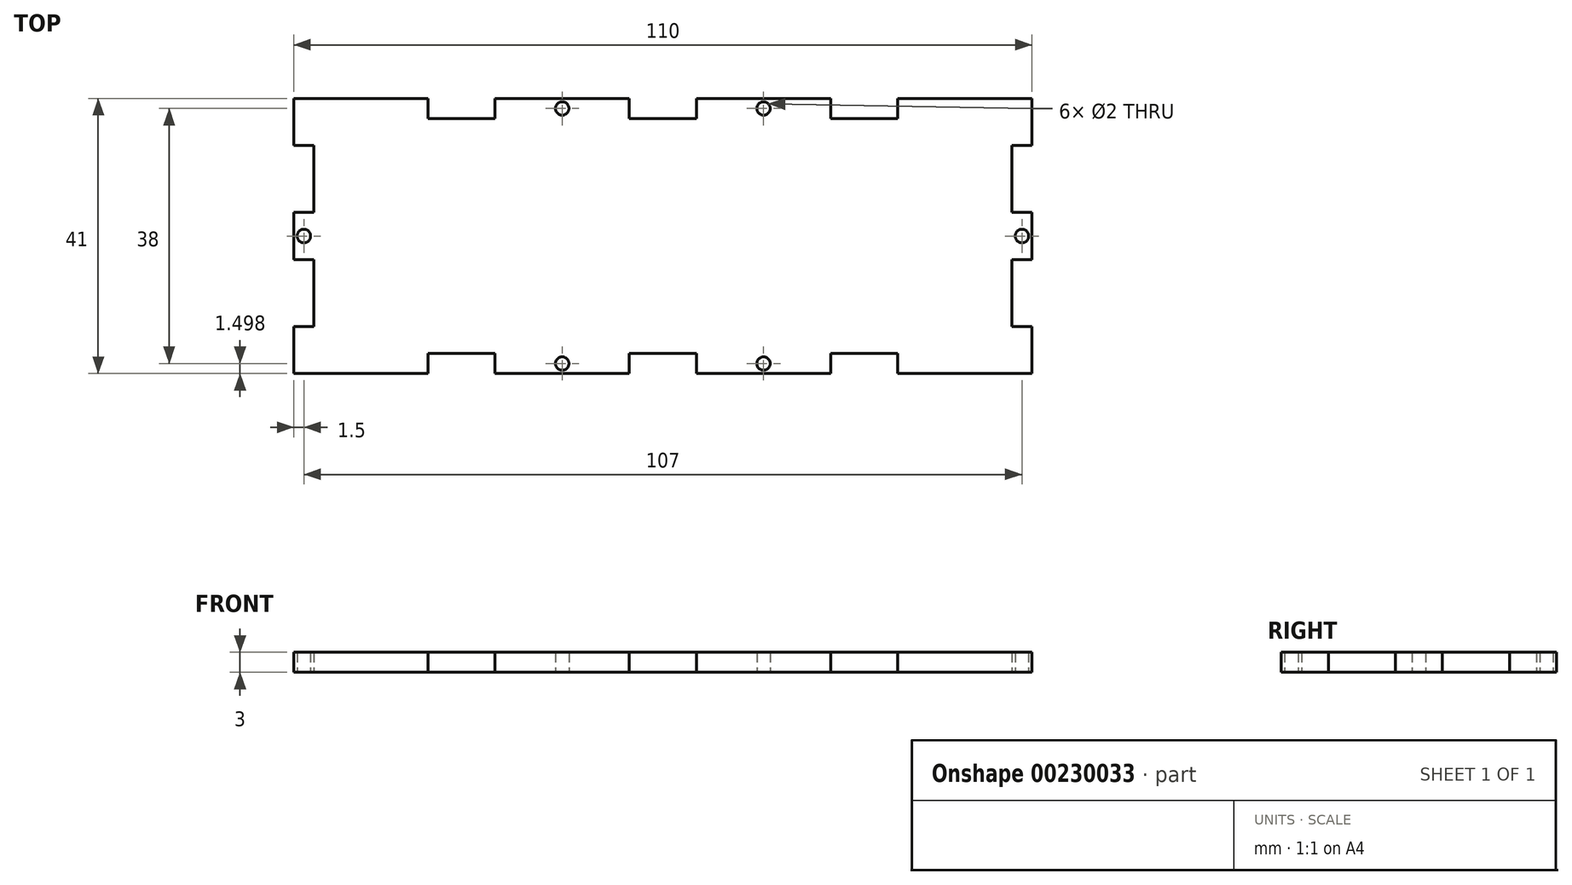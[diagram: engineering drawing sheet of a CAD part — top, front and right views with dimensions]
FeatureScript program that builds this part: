
annotation { "Feature Type Name" : "Feature", "Feature Type Description" : "" }
export const myFeature = defineFeature(function(context is Context, id is Id, definition is map)
    precondition{}
    {
        {
            var Q0;
            Q0=qCreatedBy(makeId("Top.planeOp"),FACE);
            var sketch = newSketch(context, id + "F0", { "sketchPlane" : qUnion([Q0])});
            skLineSegment(sketch, "E0", {"start": v(-55, 21.1) * mm, "end": v(-55, 14.1) * mm});
            skLineSegment(sketch, "E1", {"start": v(-55, 14.1) * mm, "end": v(-52, 14.1) * mm});
            skLineSegment(sketch, "E2", {"start": v(-52, 14.1) * mm, "end": v(-52, 4.1) * mm});
            skLineSegment(sketch, "E3", {"start": v(-52, 4.1) * mm, "end": v(-55, 4.1) * mm});
            skLineSegment(sketch, "E4", {"start": v(-55, 4.1) * mm, "end": v(-55, 0.6) * mm});
            skLineSegment(sketch, "E5", {"start": v(-55, 21.1) * mm, "end": v(-35, 21.1) * mm});
            skLineSegment(sketch, "E6", {"start": v(-35, 21.1) * mm, "end": v(-35, 18.1) * mm});
            skLineSegment(sketch, "E7", {"start": v(-35, 18.1) * mm, "end": v(-25, 18.1) * mm});
            skLineSegment(sketch, "E8", {"start": v(-25, 18.1) * mm, "end": v(-25, 21.1) * mm});
            skLineSegment(sketch, "E9", {"start": v(-25, 21.1) * mm, "end": v(-5, 21.1) * mm});
            skLineSegment(sketch, "E10", {"start": v(-5, 21.1) * mm, "end": v(-5, 18.1) * mm});
            skLineSegment(sketch, "E11", {"start": v(-5, 18.1) * mm, "end": v(0, 18.1) * mm});
            skLineSegment(sketch, "E12", {"start": v(-55, 0.6) * mm, "end": v(0, 0.6) * mm, "construction": true});
            skLineSegment(sketch, "E13.MirrorCS", {"start": v(-55, -12.9) * mm, "end": v(-52, -12.9) * mm});
            skLineSegment(sketch, "E14.MirrorCS", {"start": v(-25, -16.9) * mm, "end": v(-25, -19.9) * mm});
            skLineSegment(sketch, "E15.MirrorCS", {"start": v(-52, -2.9) * mm, "end": v(-55, -2.9) * mm});
            skLineSegment(sketch, "E16.MirrorCS", {"start": v(-55, -2.9) * mm, "end": v(-55, 0.6) * mm});
            skLineSegment(sketch, "E17.MirrorCS", {"start": v(-35, -19.9) * mm, "end": v(-35, -16.9) * mm});
            skLineSegment(sketch, "E18.MirrorCS", {"start": v(-5, -19.9) * mm, "end": v(-5, -16.9) * mm});
            skLineSegment(sketch, "E19.MirrorCS", {"start": v(-55, -19.9) * mm, "end": v(-55, -12.9) * mm});
            skLineSegment(sketch, "E20.MirrorCS", {"start": v(-5, -16.9) * mm, "end": v(0, -16.9) * mm});
            skLineSegment(sketch, "E21.MirrorCS", {"start": v(-52, -12.9) * mm, "end": v(-52, -2.9) * mm});
            skLineSegment(sketch, "E22.MirrorCS", {"start": v(-25, -19.9) * mm, "end": v(-5, -19.9) * mm});
            skLineSegment(sketch, "E23.MirrorCS", {"start": v(-55, -19.9) * mm, "end": v(-35, -19.9) * mm});
            skLineSegment(sketch, "E24.MirrorCS", {"start": v(-35, -16.9) * mm, "end": v(-25, -16.9) * mm});
            skLineSegment(sketch, "E25", {"start": v(0, 18.1) * mm, "end": v(0, -16.9) * mm, "construction": true});
            skLineSegment(sketch, "E26.MirrorCS", {"start": v(55, -2.9) * mm, "end": v(55, 0.6) * mm});
            skLineSegment(sketch, "E27.MirrorCS", {"start": v(5, 21.1) * mm, "end": v(5, 18.1) * mm});
            skLineSegment(sketch, "E28.MirrorCS", {"start": v(25, 18.1) * mm, "end": v(25, 21.1) * mm});
            skLineSegment(sketch, "E29.MirrorCS", {"start": v(35, 21.1) * mm, "end": v(35, 18.1) * mm});
            skLineSegment(sketch, "E30.MirrorCS", {"start": v(55, 4.1) * mm, "end": v(55, 0.6) * mm});
            skLineSegment(sketch, "E31.MirrorCS", {"start": v(52, 4.1) * mm, "end": v(55, 4.1) * mm});
            skLineSegment(sketch, "E32.MirrorCS", {"start": v(55, 14.1) * mm, "end": v(52, 14.1) * mm});
            skLineSegment(sketch, "E33.MirrorCS", {"start": v(25, -16.9) * mm, "end": v(25, -19.9) * mm});
            skLineSegment(sketch, "E34.MirrorCS", {"start": v(52, -2.9) * mm, "end": v(55, -2.9) * mm});
            skLineSegment(sketch, "E35.MirrorCS", {"start": v(5, -19.9) * mm, "end": v(5, -16.9) * mm});
            skLineSegment(sketch, "E36.MirrorCS", {"start": v(55, -12.9) * mm, "end": v(52, -12.9) * mm});
            skLineSegment(sketch, "E37.MirrorCS", {"start": v(35, -19.9) * mm, "end": v(35, -16.9) * mm});
            skLineSegment(sketch, "E38.MirrorCS", {"start": v(5, -16.9) * mm, "end": v(0, -16.9) * mm});
            skLineSegment(sketch, "E39.MirrorCS", {"start": v(55, -19.9) * mm, "end": v(35, -19.9) * mm});
            skLineSegment(sketch, "E40.MirrorCS", {"start": v(25, -19.9) * mm, "end": v(5, -19.9) * mm});
            skLineSegment(sketch, "E41.MirrorCS", {"start": v(55, 0.6) * mm, "end": v(0, 0.6) * mm, "construction": true});
            skLineSegment(sketch, "E42.MirrorCS", {"start": v(5, 18.1) * mm, "end": v(0, 18.1) * mm});
            skLineSegment(sketch, "E43.MirrorCS", {"start": v(25, 21.1) * mm, "end": v(5, 21.1) * mm});
            skLineSegment(sketch, "E44.MirrorCS", {"start": v(35, 18.1) * mm, "end": v(25, 18.1) * mm});
            skLineSegment(sketch, "E45.MirrorCS", {"start": v(55, 21.1) * mm, "end": v(35, 21.1) * mm});
            skLineSegment(sketch, "E46.MirrorCS", {"start": v(52, 14.1) * mm, "end": v(52, 4.1) * mm});
            skLineSegment(sketch, "E47.MirrorCS", {"start": v(55, 21.1) * mm, "end": v(55, 14.1) * mm});
            skLineSegment(sketch, "E48.MirrorCS", {"start": v(55, -19.9) * mm, "end": v(55, -12.9) * mm});
            skLineSegment(sketch, "E49.MirrorCS", {"start": v(52, -12.9) * mm, "end": v(52, -2.9) * mm});
            skLineSegment(sketch, "E50.MirrorCS", {"start": v(35, -16.9) * mm, "end": v(25, -16.9) * mm});
            skCircle(sketch, "E51", {"center": v(-15, 19.6) * mm, "radius": 1 * mm});
            skPoint(sketch, "E51.centerSnap0", {"position": v(-15, 21.1) * mm});
            skCircle(sketch, "E52.MirrorC", {"center": v(-15, -18.4) * mm, "radius": 1 * mm});
            skCircle(sketch, "E53", {"center": v(-53.5, 0.6) * mm, "radius": 1 * mm});
            skCircle(sketch, "E54.MirrorC", {"center": v(15, 19.6) * mm, "radius": 1 * mm});
            skCircle(sketch, "E55.MirrorC", {"center": v(15, -18.4) * mm, "radius": 1 * mm});
            skCircle(sketch, "E56.MirrorC", {"center": v(53.5, 0.6) * mm, "radius": 1 * mm});
            skSolve(sketch);
        }
        {
            var Q0;
            Q0 = qSketchRegion(id + "F0", true);
            extrude(context, id + "F1", {"entities" : qUnion([Q0]), "depth" : 3 * mm});
        }
    });
